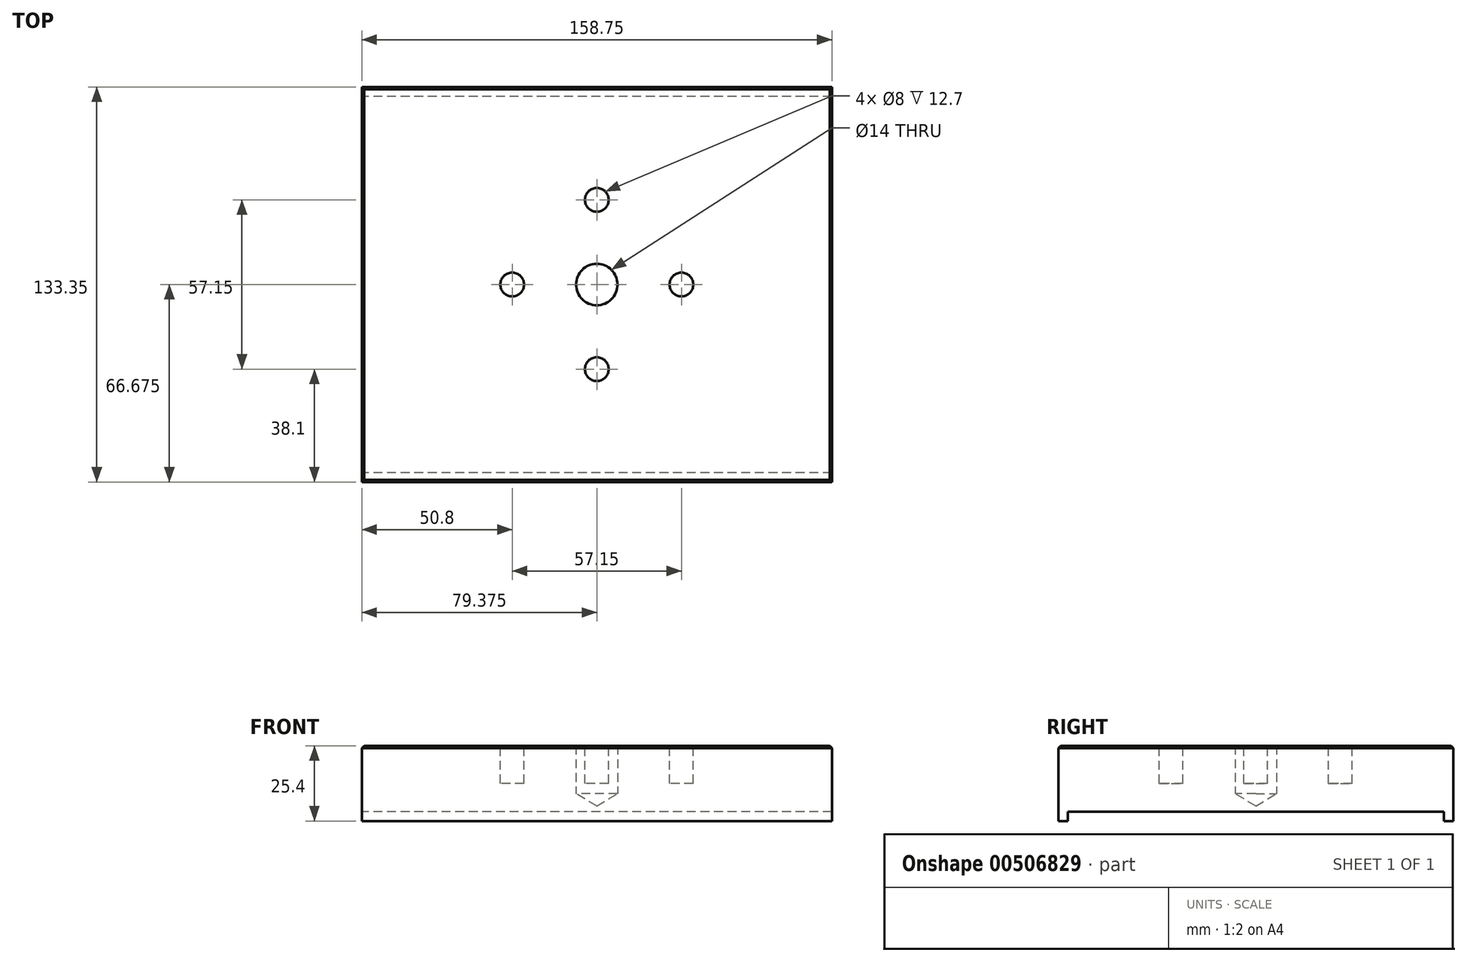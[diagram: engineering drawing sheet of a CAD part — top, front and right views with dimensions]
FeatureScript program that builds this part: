
annotation { "Feature Type Name" : "Feature", "Feature Type Description" : "" }
export const myFeature = defineFeature(function(context is Context, id is Id, definition is map)
    precondition{}
    {
        {
            var Q0;
            Q0=qCreatedBy(makeId("Right.planeOp"),FACE);
            var sketch = newSketch(context, id + "F0", { "sketchPlane" : qUnion([Q0])});
            skLineSegment(sketch, "E0.bottom", {"start": v(0, 0) * mm, "end": v(3.18, 0) * mm});
            skLineSegment(sketch, "E0.top", {"start": v(0, 25.4) * mm, "end": v(133.35, 25.4) * mm});
            skLineSegment(sketch, "E0.left", {"start": v(0, 0) * mm, "end": v(0, 25.4) * mm});
            skLineSegment(sketch, "E0.right", {"start": v(133.35, 0) * mm, "end": v(133.35, 25.4) * mm});
            skLineSegment(sketch, "E1", {"start": v(3.18, 0) * mm, "end": v(3.17, 3.18) * mm});
            skLineSegment(sketch, "E2", {"start": v(3.17, 3.18) * mm, "end": v(130.18, 3.18) * mm});
            skLineSegment(sketch, "E3", {"start": v(130.18, 3.18) * mm, "end": v(130.18, 0) * mm});
            skLineSegment(sketch, "E4.trimOffspring", {"start": v(130.18, 0) * mm, "end": v(133.35, 0) * mm});
            skSolve(sketch);
        }
        {
            var Q0;
            Q0 = qSketchRegion(id + "F0", true);
            extrude(context, id + "F1", {"entities" : qUnion([Q0]), "depth" : 158.75 * mm});
        }
        {
            var Q0;
            Q0=makeQuery(id+"F1.opExtrude","SWEPT_FACE",FACE,{"disambiguationData":[OSD([sQuery(id+"F0.wireOp",EDGE,"E0.top")])]});
            var sketch = newSketch(context, id + "F2", { "sketchPlane" : qUnion([Q0])});
            skLineSegment(sketch, "E5", {"start": v(0, 66.68) * mm, "end": v(158.75, 66.68) * mm, "construction": true});
            skPoint(sketch, "E6", {"position": v(79.38, 66.68) * mm});
            skCircle(sketch, "E7", {"center": v(79.37, 95.25) * mm, "radius": 4 * mm});
            skLineSegment(sketch, "E8", {"start": v(79.38, 66.68) * mm, "end": v(79.37, 133.35) * mm, "construction": true});
            skCircle(sketch, "E9.1.0", {"center": v(50.8, 66.67) * mm, "radius": 4 * mm});
            skCircle(sketch, "E9.2.0", {"center": v(79.38, 38.1) * mm, "radius": 4 * mm});
            skCircle(sketch, "E9.3.0", {"center": v(107.95, 66.68) * mm, "radius": 4 * mm});
            skSolve(sketch);
        }
        {
            var Q0;
            Q0 = qSketchRegion(id + "F2", true);
            extrude(context, id + "F3", {"entities" : qUnion([Q0]), "operationType" : NewBodyOperationType.REMOVE, "oppositeDirection" : true, "depth" : 12.7 * mm});
        }
        {
            var Q0;
            Q0=makeQuery(id+"F3.boolean.opBoolean","COPY",EDGE,{"derivedFrom":makeQuery(id+"F3.opExtrude","CAP_EDGE",EDGE,{"disambiguationData":[OSD([sQuery(id+"F2.wireOp",EDGE,"E7")])],"isStart":true})});
            var Q1;
            Q1=makeQuery(id+"F3.boolean.opBoolean","COPY",EDGE,{"derivedFrom":makeQuery(id+"F3.opExtrude","CAP_EDGE",EDGE,{"disambiguationData":[OSD([sQuery(id+"F2.wireOp",EDGE,"E9.3.0")])],"isStart":true})});
            var Q2;
            Q2=makeQuery(id+"F3.boolean.opBoolean","COPY",EDGE,{"derivedFrom":makeQuery(id+"F3.opExtrude","CAP_EDGE",EDGE,{"disambiguationData":[OSD([sQuery(id+"F2.wireOp",EDGE,"E9.2.0")])],"isStart":true})});
            var Q3;
            Q3=makeQuery(id+"F3.boolean.opBoolean","COPY",EDGE,{"derivedFrom":makeQuery(id+"F3.opExtrude","CAP_EDGE",EDGE,{"disambiguationData":[OSD([sQuery(id+"F2.wireOp",EDGE,"E9.1.0")])],"isStart":true})});
            var Q4;
            Q4=makeQuery(id+"F1.opExtrude","SWEPT_EDGE",EDGE,{"disambiguationData":[OSD([sQuery(id+"F0.wireOp",EDGE,"E0.top"),sQuery(id+"F0.wireOp",EDGE,"E0.right")])]});
            var Q5;
            Q5=makeQuery(id+"F1.opExtrude","CAP_EDGE",EDGE,{"disambiguationData":[OSD([sQuery(id+"F0.wireOp",EDGE,"E0.top")])],"isStart":true});
            var Q6;
            Q6=makeQuery(id+"F1.opExtrude","SWEPT_EDGE",EDGE,{"disambiguationData":[OSD([sQuery(id+"F0.wireOp",EDGE,"E0.top"),sQuery(id+"F0.wireOp",EDGE,"E0.left")])]});
            var Q7;
            Q7=makeQuery(id+"F1.opExtrude","CAP_EDGE",EDGE,{"disambiguationData":[OSD([sQuery(id+"F0.wireOp",EDGE,"E0.top")])],"isStart":false});
            chamfer(context, id + "F4", {"entities" : qUnion([Q0, Q1, Q2, Q3, Q4, Q5, Q6, Q7]), "width" : 0.76 * mm, "tangentPropagation" : true});
        }
        {
            var Q0;
            Q0=sQuery(id+"F2.wireOp",VERTEX,"E6");
            var Q1;
            Q1=makeQuery(id+"F1.opExtrude","SWEPT_BODY",BODY,{"disambiguationData":[OSD([sQuery(id+"F0.wireOp",EDGE,"E0.bottom"),sQuery(id+"F0.wireOp",EDGE,"E0.top"),sQuery(id+"F0.wireOp",EDGE,"E0.left"),sQuery(id+"F0.wireOp",EDGE,"E0.right"),sQuery(id+"F0.wireOp",EDGE,"E1"),sQuery(id+"F0.wireOp",EDGE,"E2"),sQuery(id+"F0.wireOp",EDGE,"E3"),sQuery(id+"F0.wireOp",EDGE,"E4.trimOffspring")])]});
            hole(context, id + "F5", {"style" : HoleStyle.SIMPLE, "endStyle" : HoleEndStyle.BLIND, "standardTappedOrClearance" : lookupTablePath({ "standard" : "ISO", "engagement" : "75%", "pitch" : "2 mm", "size" : "M16", "type" : "Tapped" }), "standardBlindInLast" : lookupTablePath({ "standard" : "ISO", "engagement" : "75%", "pitch" : "2 mm", "size" : "M16", "type" : "Tapped" }), "holeDiameter" : 14 * mm, "showTappedDepth" : true, "holeDepth" : 16.16 * mm, "isTappedThrough" : true, "tappedDepth" : 10.16 * mm, "tapClearance" : 3, "locations" : qUnion([Q0]), "scope" : qUnion([Q1]), "majorDiameter" : 16 * mm});
        }
    });
